# Revit family: Geräteeinsätze GES_Geräteeinsatz_GES4_mit_Griffbügel
name_source: partatom
category: Generic Models
revit_build: Autodesk Revit 2015 (Build: 20140606_1530(x64)
units: mm (PartAtom-declared; Revit-internal decimal feet)

## types (3) — shared parameters
Height = 61 mm  [stored 0.200131 ft]
Manufacturer = OBO Bettermann
Snur width = 77 mm  [stored 0.252625 ft]
URL = http://www.obo-bettermann.com
Width = 217 mm  [stored 0.711942 ft]
Width 2 = 200 mm  [stored 0.656168 ft]

## per-type parameters (varying)
| type | Article Type | GTIN | Manufacturer Art. No. | Material |
| GES4 U 9011 | GES4 U 9011 | 4012195102595 | 74052000 | Plastic RAL 9011 |
| GES4 U 7011 | GES4 U 7011 | 4012195102182
4012195102588 | 7405196 | Plastic RAL 7011 |
| GES2 U 1019 | GES4 U 1019 | 4012195102601 | 7405204 | Plastic RAL 1019 |

note: [stored X ft] marks values corroborated as IEEE doubles in the binary element streams (Revit-internal decimal feet)

## geometry (parser evidence)
native form markers: Sweep x2
no freeform markers — native parametric forms only
